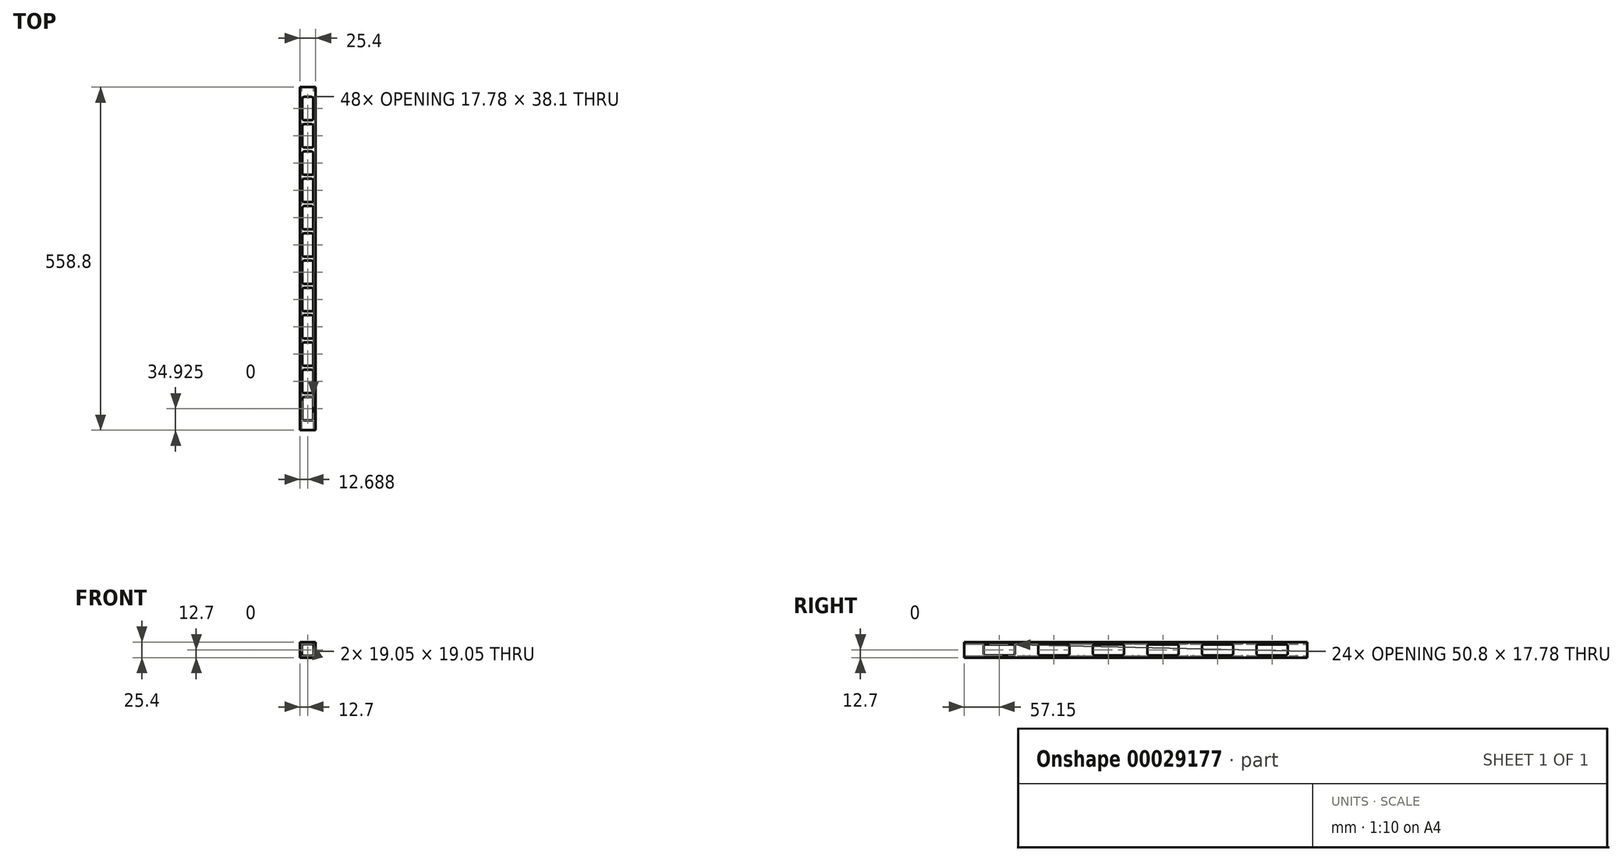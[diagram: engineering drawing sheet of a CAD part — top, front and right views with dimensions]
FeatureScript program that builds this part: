
annotation { "Feature Type Name" : "Feature", "Feature Type Description" : "" }
export const myFeature = defineFeature(function(context is Context, id is Id, definition is map)
    precondition{}
    {
        {
            var Q0;
            Q0=qCreatedBy(makeId("Front.planeOp"),FACE);
            var sketch = newSketch(context, id + "F0", { "sketchPlane" : qUnion([Q0])});
            skLineSegment(sketch, "E0.rect.bottom", {"start": v(12.7, 12.7) * mm, "end": v(-12.7, 12.7) * mm});
            skLineSegment(sketch, "E0.rect.top", {"start": v(12.7, -12.7) * mm, "end": v(-12.7, -12.7) * mm});
            skLineSegment(sketch, "E0.rect.left", {"start": v(12.7, 12.7) * mm, "end": v(12.7, -12.7) * mm});
            skLineSegment(sketch, "E0.rect.right", {"start": v(-12.7, 12.7) * mm, "end": v(-12.7, -12.7) * mm});
            skPoint(sketch, "E0.rect.middle", {"position": v(0, 0) * mm});
            skLineSegment(sketch, "E1.rect.bottom", {"start": v(9.53, 9.53) * mm, "end": v(-9.53, 9.53) * mm});
            skLineSegment(sketch, "E1.rect.top", {"start": v(9.53, -9.53) * mm, "end": v(-9.53, -9.53) * mm});
            skLineSegment(sketch, "E1.rect.left", {"start": v(9.53, 9.53) * mm, "end": v(9.53, -9.53) * mm});
            skLineSegment(sketch, "E1.rect.right", {"start": v(-9.53, 9.53) * mm, "end": v(-9.53, -9.53) * mm});
            skSolve(sketch);
        }
        {
            var Q0;
            Q0=qSketchRegion(id+"F0",true);
            extrude(context, id + "F1", {"entities" : qUnion([Q0]), "depth" : 558.8 * mm});
        }
        {
            var Q0;
            Q0=makeQuery(id+"F1.opExtrude","SWEPT_FACE",FACE,{"disambiguationData":[OSD([sQuery(id+"F0.wireOp",EDGE,"E0.rect.bottom")])]});
            var sketch = newSketch(context, id + "F2", { "sketchPlane" : qUnion([Q0])});
            skLineSegment(sketch, "E2.rect.bottom", {"start": v(5.7, -504.83) * mm, "end": v(-5.73, -504.83) * mm});
            skLineSegment(sketch, "E2.rect.top", {"start": v(5.7, -542.93) * mm, "end": v(-5.73, -542.93) * mm});
            skLineSegment(sketch, "E2.rect.left", {"start": v(8.88, -508) * mm, "end": v(8.88, -539.75) * mm});
            skLineSegment(sketch, "E2.rect.right", {"start": v(-8.9, -508) * mm, "end": v(-8.9, -539.75) * mm});
            skPoint(sketch, "E2.rect.middle", {"position": v(-0.01, -523.88) * mm});
            skPoint(sketch, "E3.visualSharp", {"position": v(-8.9, -504.83) * mm});
            skArc(sketch, "E3.filletArc", {"start": v(-5.73, -504.82) * mm, "mid": v(-7.97, -505.75) * mm, "end": v(-8.9, -508) * mm});
            skPoint(sketch, "E4.visualSharp", {"position": v(8.88, -542.93) * mm});
            skArc(sketch, "E4.filletArc", {"start": v(5.7, -542.93) * mm, "mid": v(7.95, -542) * mm, "end": v(8.88, -539.75) * mm});
            skPoint(sketch, "E5.visualSharp", {"position": v(-8.9, -542.93) * mm});
            skArc(sketch, "E5.filletArc", {"start": v(-8.9, -539.75) * mm, "mid": v(-7.97, -542) * mm, "end": v(-5.73, -542.93) * mm});
            skPoint(sketch, "E6.visualSharp", {"position": v(8.88, -504.83) * mm});
            skArc(sketch, "E6.filletArc", {"start": v(8.88, -508) * mm, "mid": v(7.95, -505.75) * mm, "end": v(5.7, -504.82) * mm});
            skLineSegment(sketch, "E7.0.1.0", {"start": v(5.7, -460.38) * mm, "end": v(-5.73, -460.38) * mm});
            skArc(sketch, "E7.0.1.1", {"start": v(-5.73, -460.38) * mm, "mid": v(-7.97, -461.3) * mm, "end": v(-8.9, -463.55) * mm});
            skLineSegment(sketch, "E7.0.1.2", {"start": v(-8.9, -463.55) * mm, "end": v(-8.9, -495.3) * mm});
            skArc(sketch, "E7.0.1.3", {"start": v(-8.9, -495.3) * mm, "mid": v(-7.97, -497.55) * mm, "end": v(-5.73, -498.48) * mm});
            skLineSegment(sketch, "E7.0.1.4", {"start": v(5.7, -498.48) * mm, "end": v(-5.73, -498.48) * mm});
            skArc(sketch, "E7.0.1.5", {"start": v(5.7, -498.48) * mm, "mid": v(7.95, -497.55) * mm, "end": v(8.88, -495.3) * mm});
            skLineSegment(sketch, "E7.0.1.6", {"start": v(8.88, -463.55) * mm, "end": v(8.88, -495.3) * mm});
            skArc(sketch, "E7.0.1.7", {"start": v(8.88, -463.55) * mm, "mid": v(7.95, -461.3) * mm, "end": v(5.7, -460.38) * mm});
            skLineSegment(sketch, "E7.0.2.0", {"start": v(5.7, -415.93) * mm, "end": v(-5.73, -415.93) * mm});
            skArc(sketch, "E7.0.2.1", {"start": v(-5.73, -415.93) * mm, "mid": v(-7.97, -416.85) * mm, "end": v(-8.9, -419.1) * mm});
            skLineSegment(sketch, "E7.0.2.2", {"start": v(-8.9, -419.1) * mm, "end": v(-8.9, -450.85) * mm});
            skArc(sketch, "E7.0.2.3", {"start": v(-8.9, -450.85) * mm, "mid": v(-7.97, -453.1) * mm, "end": v(-5.73, -454.03) * mm});
            skLineSegment(sketch, "E7.0.2.4", {"start": v(5.7, -454.03) * mm, "end": v(-5.73, -454.03) * mm});
            skArc(sketch, "E7.0.2.5", {"start": v(5.7, -454.03) * mm, "mid": v(7.95, -453.1) * mm, "end": v(8.88, -450.85) * mm});
            skLineSegment(sketch, "E7.0.2.6", {"start": v(8.88, -419.1) * mm, "end": v(8.88, -450.85) * mm});
            skArc(sketch, "E7.0.2.7", {"start": v(8.88, -419.1) * mm, "mid": v(7.95, -416.85) * mm, "end": v(5.7, -415.93) * mm});
            skLineSegment(sketch, "E7.0.3.0", {"start": v(5.7, -371.48) * mm, "end": v(-5.73, -371.48) * mm});
            skArc(sketch, "E7.0.3.1", {"start": v(-5.73, -371.48) * mm, "mid": v(-7.97, -372.4) * mm, "end": v(-8.9, -374.65) * mm});
            skLineSegment(sketch, "E7.0.3.2", {"start": v(-8.9, -374.65) * mm, "end": v(-8.9, -406.4) * mm});
            skArc(sketch, "E7.0.3.3", {"start": v(-8.9, -406.4) * mm, "mid": v(-7.97, -408.65) * mm, "end": v(-5.73, -409.58) * mm});
            skLineSegment(sketch, "E7.0.3.4", {"start": v(5.7, -409.58) * mm, "end": v(-5.73, -409.58) * mm});
            skArc(sketch, "E7.0.3.5", {"start": v(5.7, -409.58) * mm, "mid": v(7.95, -408.65) * mm, "end": v(8.88, -406.4) * mm});
            skLineSegment(sketch, "E7.0.3.6", {"start": v(8.88, -374.65) * mm, "end": v(8.88, -406.4) * mm});
            skArc(sketch, "E7.0.3.7", {"start": v(8.88, -374.65) * mm, "mid": v(7.95, -372.4) * mm, "end": v(5.7, -371.48) * mm});
            skLineSegment(sketch, "E7.0.4.0", {"start": v(5.7, -327.03) * mm, "end": v(-5.73, -327.03) * mm});
            skArc(sketch, "E7.0.4.1", {"start": v(-5.73, -327.03) * mm, "mid": v(-7.97, -327.95) * mm, "end": v(-8.9, -330.2) * mm});
            skLineSegment(sketch, "E7.0.4.2", {"start": v(-8.9, -330.2) * mm, "end": v(-8.9, -361.95) * mm});
            skArc(sketch, "E7.0.4.3", {"start": v(-8.9, -361.95) * mm, "mid": v(-7.97, -364.2) * mm, "end": v(-5.73, -365.13) * mm});
            skLineSegment(sketch, "E7.0.4.4", {"start": v(5.7, -365.13) * mm, "end": v(-5.73, -365.13) * mm});
            skArc(sketch, "E7.0.4.5", {"start": v(5.7, -365.13) * mm, "mid": v(7.95, -364.2) * mm, "end": v(8.88, -361.95) * mm});
            skLineSegment(sketch, "E7.0.4.6", {"start": v(8.88, -330.2) * mm, "end": v(8.88, -361.95) * mm});
            skArc(sketch, "E7.0.4.7", {"start": v(8.88, -330.2) * mm, "mid": v(7.95, -327.95) * mm, "end": v(5.7, -327.03) * mm});
            skLineSegment(sketch, "E7.0.5.0", {"start": v(5.7, -282.58) * mm, "end": v(-5.73, -282.58) * mm});
            skArc(sketch, "E7.0.5.1", {"start": v(-5.73, -282.58) * mm, "mid": v(-7.97, -283.5) * mm, "end": v(-8.9, -285.75) * mm});
            skLineSegment(sketch, "E7.0.5.2", {"start": v(-8.9, -285.75) * mm, "end": v(-8.9, -317.5) * mm});
            skArc(sketch, "E7.0.5.3", {"start": v(-8.9, -317.5) * mm, "mid": v(-7.97, -319.75) * mm, "end": v(-5.73, -320.68) * mm});
            skLineSegment(sketch, "E7.0.5.4", {"start": v(5.7, -320.68) * mm, "end": v(-5.73, -320.68) * mm});
            skArc(sketch, "E7.0.5.5", {"start": v(5.7, -320.68) * mm, "mid": v(7.95, -319.75) * mm, "end": v(8.88, -317.5) * mm});
            skLineSegment(sketch, "E7.0.5.6", {"start": v(8.88, -285.75) * mm, "end": v(8.88, -317.5) * mm});
            skArc(sketch, "E7.0.5.7", {"start": v(8.88, -285.75) * mm, "mid": v(7.95, -283.5) * mm, "end": v(5.7, -282.58) * mm});
            skLineSegment(sketch, "E7.0.6.0", {"start": v(5.7, -238.13) * mm, "end": v(-5.73, -238.13) * mm});
            skArc(sketch, "E7.0.6.1", {"start": v(-5.73, -238.13) * mm, "mid": v(-7.97, -239.05) * mm, "end": v(-8.9, -241.3) * mm});
            skLineSegment(sketch, "E7.0.6.2", {"start": v(-8.9, -241.3) * mm, "end": v(-8.9, -273.05) * mm});
            skArc(sketch, "E7.0.6.3", {"start": v(-8.9, -273.05) * mm, "mid": v(-7.97, -275.3) * mm, "end": v(-5.73, -276.23) * mm});
            skLineSegment(sketch, "E7.0.6.4", {"start": v(5.7, -276.23) * mm, "end": v(-5.73, -276.23) * mm});
            skArc(sketch, "E7.0.6.5", {"start": v(5.7, -276.23) * mm, "mid": v(7.95, -275.3) * mm, "end": v(8.88, -273.05) * mm});
            skLineSegment(sketch, "E7.0.6.6", {"start": v(8.88, -241.3) * mm, "end": v(8.88, -273.05) * mm});
            skArc(sketch, "E7.0.6.7", {"start": v(8.88, -241.3) * mm, "mid": v(7.95, -239.05) * mm, "end": v(5.7, -238.13) * mm});
            skLineSegment(sketch, "E7.0.7.0", {"start": v(5.7, -193.68) * mm, "end": v(-5.73, -193.68) * mm});
            skArc(sketch, "E7.0.7.1", {"start": v(-5.73, -193.68) * mm, "mid": v(-7.97, -194.6) * mm, "end": v(-8.9, -196.85) * mm});
            skLineSegment(sketch, "E7.0.7.2", {"start": v(-8.9, -196.85) * mm, "end": v(-8.9, -228.6) * mm});
            skArc(sketch, "E7.0.7.3", {"start": v(-8.9, -228.6) * mm, "mid": v(-7.97, -230.85) * mm, "end": v(-5.73, -231.78) * mm});
            skLineSegment(sketch, "E7.0.7.4", {"start": v(5.7, -231.78) * mm, "end": v(-5.73, -231.78) * mm});
            skArc(sketch, "E7.0.7.5", {"start": v(5.7, -231.78) * mm, "mid": v(7.95, -230.85) * mm, "end": v(8.88, -228.6) * mm});
            skLineSegment(sketch, "E7.0.7.6", {"start": v(8.88, -196.85) * mm, "end": v(8.88, -228.6) * mm});
            skArc(sketch, "E7.0.7.7", {"start": v(8.88, -196.85) * mm, "mid": v(7.95, -194.6) * mm, "end": v(5.7, -193.68) * mm});
            skLineSegment(sketch, "E7.0.8.0", {"start": v(5.7, -149.23) * mm, "end": v(-5.73, -149.23) * mm});
            skArc(sketch, "E7.0.8.1", {"start": v(-5.73, -149.23) * mm, "mid": v(-7.97, -150.15) * mm, "end": v(-8.9, -152.4) * mm});
            skLineSegment(sketch, "E7.0.8.2", {"start": v(-8.9, -152.4) * mm, "end": v(-8.9, -184.15) * mm});
            skArc(sketch, "E7.0.8.3", {"start": v(-8.9, -184.15) * mm, "mid": v(-7.97, -186.4) * mm, "end": v(-5.73, -187.33) * mm});
            skLineSegment(sketch, "E7.0.8.4", {"start": v(5.7, -187.33) * mm, "end": v(-5.73, -187.33) * mm});
            skArc(sketch, "E7.0.8.5", {"start": v(5.7, -187.33) * mm, "mid": v(7.95, -186.4) * mm, "end": v(8.88, -184.15) * mm});
            skLineSegment(sketch, "E7.0.8.6", {"start": v(8.88, -152.4) * mm, "end": v(8.88, -184.15) * mm});
            skArc(sketch, "E7.0.8.7", {"start": v(8.88, -152.4) * mm, "mid": v(7.95, -150.15) * mm, "end": v(5.7, -149.23) * mm});
            skLineSegment(sketch, "E7.0.9.0", {"start": v(5.7, -104.78) * mm, "end": v(-5.73, -104.78) * mm});
            skArc(sketch, "E7.0.9.1", {"start": v(-5.73, -104.78) * mm, "mid": v(-7.97, -105.7) * mm, "end": v(-8.9, -107.95) * mm});
            skLineSegment(sketch, "E7.0.9.2", {"start": v(-8.9, -107.95) * mm, "end": v(-8.9, -139.7) * mm});
            skArc(sketch, "E7.0.9.3", {"start": v(-8.9, -139.7) * mm, "mid": v(-7.97, -141.95) * mm, "end": v(-5.73, -142.88) * mm});
            skLineSegment(sketch, "E7.0.9.4", {"start": v(5.7, -142.88) * mm, "end": v(-5.73, -142.88) * mm});
            skArc(sketch, "E7.0.9.5", {"start": v(5.7, -142.88) * mm, "mid": v(7.95, -141.95) * mm, "end": v(8.88, -139.7) * mm});
            skLineSegment(sketch, "E7.0.9.6", {"start": v(8.88, -107.95) * mm, "end": v(8.88, -139.7) * mm});
            skArc(sketch, "E7.0.9.7", {"start": v(8.88, -107.95) * mm, "mid": v(7.95, -105.7) * mm, "end": v(5.7, -104.78) * mm});
            skLineSegment(sketch, "E7.0.10.0", {"start": v(5.7, -60.33) * mm, "end": v(-5.73, -60.33) * mm});
            skArc(sketch, "E7.0.10.1", {"start": v(-5.73, -60.33) * mm, "mid": v(-7.97, -61.25) * mm, "end": v(-8.9, -63.5) * mm});
            skLineSegment(sketch, "E7.0.10.2", {"start": v(-8.9, -63.5) * mm, "end": v(-8.9, -95.25) * mm});
            skArc(sketch, "E7.0.10.3", {"start": v(-8.9, -95.25) * mm, "mid": v(-7.97, -97.5) * mm, "end": v(-5.73, -98.43) * mm});
            skLineSegment(sketch, "E7.0.10.4", {"start": v(5.7, -98.43) * mm, "end": v(-5.73, -98.43) * mm});
            skArc(sketch, "E7.0.10.5", {"start": v(5.7, -98.43) * mm, "mid": v(7.95, -97.5) * mm, "end": v(8.88, -95.25) * mm});
            skLineSegment(sketch, "E7.0.10.6", {"start": v(8.88, -63.5) * mm, "end": v(8.88, -95.25) * mm});
            skArc(sketch, "E7.0.10.7", {"start": v(8.88, -63.5) * mm, "mid": v(7.95, -61.25) * mm, "end": v(5.7, -60.33) * mm});
            skLineSegment(sketch, "E7.0.11.0", {"start": v(5.7, -15.88) * mm, "end": v(-5.73, -15.88) * mm});
            skArc(sketch, "E7.0.11.1", {"start": v(-5.73, -15.88) * mm, "mid": v(-7.97, -16.8) * mm, "end": v(-8.9, -19.05) * mm});
            skLineSegment(sketch, "E7.0.11.2", {"start": v(-8.9, -19.05) * mm, "end": v(-8.9, -50.8) * mm});
            skArc(sketch, "E7.0.11.3", {"start": v(-8.9, -50.8) * mm, "mid": v(-7.97, -53.05) * mm, "end": v(-5.73, -53.98) * mm});
            skLineSegment(sketch, "E7.0.11.4", {"start": v(5.7, -53.98) * mm, "end": v(-5.73, -53.98) * mm});
            skArc(sketch, "E7.0.11.5", {"start": v(5.7, -53.98) * mm, "mid": v(7.95, -53.05) * mm, "end": v(8.88, -50.8) * mm});
            skLineSegment(sketch, "E7.0.11.6", {"start": v(8.88, -19.05) * mm, "end": v(8.88, -50.8) * mm});
            skArc(sketch, "E7.0.11.7", {"start": v(8.88, -19.05) * mm, "mid": v(7.95, -16.8) * mm, "end": v(5.7, -15.88) * mm});
            skLineSegment(sketch, "E7.direction1", {"start": v(-5.73, -504.83) * mm, "end": v(19.67, -504.83) * mm, "construction": true});
            skLineSegment(sketch, "E7.direction2", {"start": v(-5.73, -504.83) * mm, "end": v(-5.73, -460.38) * mm, "construction": true});
            skSolve(sketch);
        }
        {
            var Q0;
            Q0=makeQuery(id+"F2.imprint","IMPRINT",FACE,{"disambiguationData":[TD([[makeQuery(id+"F2.imprint","IMPRINT",EDGE,{"derivedFrom":sQuery(id+"F2.wireOp",EDGE,"E2.rect.bottom")}),1.0]])]});
            var Q1;
            Q1=makeQuery(id+"F2.imprint","IMPRINT",FACE,{"disambiguationData":[TD([[makeQuery(id+"F2.imprint","IMPRINT",EDGE,{"derivedFrom":sQuery(id+"F2.wireOp",EDGE,"E7.0.1.0")}),1.0]])]});
            var Q2;
            Q2=makeQuery(id+"F2.imprint","IMPRINT",FACE,{"disambiguationData":[TD([[makeQuery(id+"F2.imprint","IMPRINT",EDGE,{"derivedFrom":sQuery(id+"F2.wireOp",EDGE,"E7.0.2.0")}),1.0]])]});
            var Q3;
            Q3=makeQuery(id+"F2.imprint","IMPRINT",FACE,{"disambiguationData":[TD([[makeQuery(id+"F2.imprint","IMPRINT",EDGE,{"derivedFrom":sQuery(id+"F2.wireOp",EDGE,"E7.0.3.0")}),1.0]])]});
            var Q4;
            Q4=makeQuery(id+"F2.imprint","IMPRINT",FACE,{"disambiguationData":[TD([[makeQuery(id+"F2.imprint","IMPRINT",EDGE,{"derivedFrom":sQuery(id+"F2.wireOp",EDGE,"E7.0.4.0")}),1.0]])]});
            var Q5;
            Q5=makeQuery(id+"F2.imprint","IMPRINT",FACE,{"disambiguationData":[TD([[makeQuery(id+"F2.imprint","IMPRINT",EDGE,{"derivedFrom":sQuery(id+"F2.wireOp",EDGE,"E7.0.5.0")}),1.0]])]});
            var Q6;
            Q6=makeQuery(id+"F2.imprint","IMPRINT",FACE,{"disambiguationData":[TD([[makeQuery(id+"F2.imprint","IMPRINT",EDGE,{"derivedFrom":sQuery(id+"F2.wireOp",EDGE,"E7.0.6.0")}),1.0]])]});
            var Q7;
            Q7=makeQuery(id+"F2.imprint","IMPRINT",FACE,{"disambiguationData":[TD([[makeQuery(id+"F2.imprint","IMPRINT",EDGE,{"derivedFrom":sQuery(id+"F2.wireOp",EDGE,"E7.0.7.0")}),1.0]])]});
            var Q8;
            Q8=makeQuery(id+"F2.imprint","IMPRINT",FACE,{"disambiguationData":[TD([[makeQuery(id+"F2.imprint","IMPRINT",EDGE,{"derivedFrom":sQuery(id+"F2.wireOp",EDGE,"E7.0.8.0")}),1.0]])]});
            var Q9;
            Q9=makeQuery(id+"F2.imprint","IMPRINT",FACE,{"disambiguationData":[TD([[makeQuery(id+"F2.imprint","IMPRINT",EDGE,{"derivedFrom":sQuery(id+"F2.wireOp",EDGE,"E7.0.9.0")}),1.0]])]});
            var Q10;
            Q10=makeQuery(id+"F2.imprint","IMPRINT",FACE,{"disambiguationData":[TD([[makeQuery(id+"F2.imprint","IMPRINT",EDGE,{"derivedFrom":sQuery(id+"F2.wireOp",EDGE,"E7.0.10.0")}),1.0]])]});
            var Q11;
            Q11=makeQuery(id+"F2.imprint","IMPRINT",FACE,{"disambiguationData":[TD([[makeQuery(id+"F2.imprint","IMPRINT",EDGE,{"derivedFrom":sQuery(id+"F2.wireOp",EDGE,"E7.0.11.0")}),1.0]])]});
            extrude(context, id + "F3", {"entities" : qUnion([Q0, Q1, Q2, Q3, Q4, Q5, Q6, Q7, Q8, Q9, Q10, Q11]), "operationType" : NewBodyOperationType.REMOVE, "oppositeDirection" : true, "depth" : 25.4 * mm});
        }
        {
            var Q0;
            Q0=makeQuery(id+"F1.opExtrude","SWEPT_FACE",FACE,{"disambiguationData":[OSD([sQuery(id+"F0.wireOp",EDGE,"E0.rect.left")])]});
            var sketch = newSketch(context, id + "F4", { "sketchPlane" : qUnion([Q0])});
            skLineSegment(sketch, "E8", {"start": v(-558.8, 0) * mm, "end": v(-527.05, 0) * mm});
            skLineSegment(sketch, "E9.rect.bottom", {"start": v(-479.43, -8.89) * mm, "end": v(-523.88, -8.89) * mm});
            skLineSegment(sketch, "E9.rect.top", {"start": v(-479.43, 8.9) * mm, "end": v(-523.88, 8.9) * mm});
            skLineSegment(sketch, "E9.rect.left", {"start": v(-476.25, -5.71) * mm, "end": v(-476.25, 5.72) * mm});
            skLineSegment(sketch, "E9.rect.right", {"start": v(-527.05, -5.71) * mm, "end": v(-527.05, 5.72) * mm});
            skPoint(sketch, "E9.rect.middle", {"position": v(-501.65, 0) * mm});
            skPoint(sketch, "E10.visualSharp", {"position": v(-476.25, 8.9) * mm});
            skArc(sketch, "E10.filletArc", {"start": v(-476.25, 5.72) * mm, "mid": v(-477.18, 7.96) * mm, "end": v(-479.43, 8.9) * mm});
            skPoint(sketch, "E11.visualSharp", {"position": v(-476.25, -8.89) * mm});
            skArc(sketch, "E11.filletArc", {"start": v(-479.43, -8.89) * mm, "mid": v(-477.18, -7.96) * mm, "end": v(-476.25, -5.71) * mm});
            skPoint(sketch, "E12.visualSharp", {"position": v(-527.05, -8.89) * mm});
            skArc(sketch, "E12.filletArc", {"start": v(-527.05, -5.71) * mm, "mid": v(-526.12, -7.96) * mm, "end": v(-523.88, -8.89) * mm});
            skPoint(sketch, "E13.visualSharp", {"position": v(-527.05, 8.9) * mm});
            skArc(sketch, "E13.filletArc", {"start": v(-523.88, 8.9) * mm, "mid": v(-526.12, 7.96) * mm, "end": v(-527.05, 5.72) * mm});
            skLineSegment(sketch, "E14.1.0.0", {"start": v(-387.35, -5.71) * mm, "end": v(-387.35, 5.72) * mm});
            skArc(sketch, "E14.1.0.1", {"start": v(-387.35, 5.72) * mm, "mid": v(-388.28, 7.96) * mm, "end": v(-390.52, 8.9) * mm});
            skLineSegment(sketch, "E14.1.0.2", {"start": v(-390.52, 8.9) * mm, "end": v(-434.97, 8.9) * mm});
            skArc(sketch, "E14.1.0.3", {"start": v(-434.97, 8.9) * mm, "mid": v(-437.22, 7.96) * mm, "end": v(-438.15, 5.72) * mm});
            skLineSegment(sketch, "E14.1.0.4", {"start": v(-438.15, -5.71) * mm, "end": v(-438.15, 5.72) * mm});
            skArc(sketch, "E14.1.0.5", {"start": v(-438.15, -5.71) * mm, "mid": v(-437.22, -7.96) * mm, "end": v(-434.97, -8.89) * mm});
            skLineSegment(sketch, "E14.1.0.6", {"start": v(-390.52, -8.89) * mm, "end": v(-434.97, -8.89) * mm});
            skArc(sketch, "E14.1.0.7", {"start": v(-390.52, -8.89) * mm, "mid": v(-388.28, -7.96) * mm, "end": v(-387.35, -5.71) * mm});
            skLineSegment(sketch, "E14.2.0.0", {"start": v(-298.45, -5.71) * mm, "end": v(-298.45, 5.72) * mm});
            skArc(sketch, "E14.2.0.1", {"start": v(-298.45, 5.72) * mm, "mid": v(-299.38, 7.96) * mm, "end": v(-301.62, 8.9) * mm});
            skLineSegment(sketch, "E14.2.0.2", {"start": v(-301.62, 8.9) * mm, "end": v(-346.07, 8.9) * mm});
            skArc(sketch, "E14.2.0.3", {"start": v(-346.07, 8.9) * mm, "mid": v(-348.32, 7.96) * mm, "end": v(-349.25, 5.72) * mm});
            skLineSegment(sketch, "E14.2.0.4", {"start": v(-349.25, -5.71) * mm, "end": v(-349.25, 5.72) * mm});
            skArc(sketch, "E14.2.0.5", {"start": v(-349.25, -5.71) * mm, "mid": v(-348.32, -7.96) * mm, "end": v(-346.07, -8.89) * mm});
            skLineSegment(sketch, "E14.2.0.6", {"start": v(-301.62, -8.89) * mm, "end": v(-346.07, -8.89) * mm});
            skArc(sketch, "E14.2.0.7", {"start": v(-301.62, -8.89) * mm, "mid": v(-299.38, -7.96) * mm, "end": v(-298.45, -5.71) * mm});
            skLineSegment(sketch, "E14.3.0.0", {"start": v(-209.55, -5.71) * mm, "end": v(-209.55, 5.72) * mm});
            skArc(sketch, "E14.3.0.1", {"start": v(-209.55, 5.72) * mm, "mid": v(-210.48, 7.96) * mm, "end": v(-212.72, 8.9) * mm});
            skLineSegment(sketch, "E14.3.0.2", {"start": v(-212.72, 8.9) * mm, "end": v(-257.17, 8.9) * mm});
            skArc(sketch, "E14.3.0.3", {"start": v(-257.17, 8.9) * mm, "mid": v(-259.42, 7.96) * mm, "end": v(-260.35, 5.72) * mm});
            skLineSegment(sketch, "E14.3.0.4", {"start": v(-260.35, -5.71) * mm, "end": v(-260.35, 5.72) * mm});
            skArc(sketch, "E14.3.0.5", {"start": v(-260.35, -5.71) * mm, "mid": v(-259.42, -7.96) * mm, "end": v(-257.17, -8.89) * mm});
            skLineSegment(sketch, "E14.3.0.6", {"start": v(-212.72, -8.89) * mm, "end": v(-257.17, -8.89) * mm});
            skArc(sketch, "E14.3.0.7", {"start": v(-212.72, -8.89) * mm, "mid": v(-210.48, -7.96) * mm, "end": v(-209.55, -5.71) * mm});
            skLineSegment(sketch, "E14.4.0.0", {"start": v(-120.65, -5.71) * mm, "end": v(-120.65, 5.72) * mm});
            skArc(sketch, "E14.4.0.1", {"start": v(-120.65, 5.72) * mm, "mid": v(-121.58, 7.96) * mm, "end": v(-123.82, 8.9) * mm});
            skLineSegment(sketch, "E14.4.0.2", {"start": v(-123.82, 8.9) * mm, "end": v(-168.27, 8.9) * mm});
            skArc(sketch, "E14.4.0.3", {"start": v(-168.27, 8.9) * mm, "mid": v(-170.52, 7.96) * mm, "end": v(-171.45, 5.72) * mm});
            skLineSegment(sketch, "E14.4.0.4", {"start": v(-171.45, -5.71) * mm, "end": v(-171.45, 5.72) * mm});
            skArc(sketch, "E14.4.0.5", {"start": v(-171.45, -5.71) * mm, "mid": v(-170.52, -7.96) * mm, "end": v(-168.27, -8.89) * mm});
            skLineSegment(sketch, "E14.4.0.6", {"start": v(-123.82, -8.89) * mm, "end": v(-168.27, -8.89) * mm});
            skArc(sketch, "E14.4.0.7", {"start": v(-123.82, -8.89) * mm, "mid": v(-121.58, -7.96) * mm, "end": v(-120.65, -5.71) * mm});
            skLineSegment(sketch, "E14.5.0.0", {"start": v(-31.75, -5.71) * mm, "end": v(-31.75, 5.72) * mm});
            skArc(sketch, "E14.5.0.1", {"start": v(-31.75, 5.72) * mm, "mid": v(-32.68, 7.96) * mm, "end": v(-34.92, 8.9) * mm});
            skLineSegment(sketch, "E14.5.0.2", {"start": v(-34.92, 8.9) * mm, "end": v(-79.37, 8.9) * mm});
            skArc(sketch, "E14.5.0.3", {"start": v(-79.37, 8.9) * mm, "mid": v(-81.62, 7.96) * mm, "end": v(-82.55, 5.72) * mm});
            skLineSegment(sketch, "E14.5.0.4", {"start": v(-82.55, -5.71) * mm, "end": v(-82.55, 5.72) * mm});
            skArc(sketch, "E14.5.0.5", {"start": v(-82.55, -5.71) * mm, "mid": v(-81.62, -7.96) * mm, "end": v(-79.37, -8.89) * mm});
            skLineSegment(sketch, "E14.5.0.6", {"start": v(-34.92, -8.89) * mm, "end": v(-79.37, -8.89) * mm});
            skArc(sketch, "E14.5.0.7", {"start": v(-34.92, -8.89) * mm, "mid": v(-32.68, -7.96) * mm, "end": v(-31.75, -5.71) * mm});
            skLineSegment(sketch, "E14.direction1", {"start": v(-476.25, -5.71) * mm, "end": v(-387.35, -5.71) * mm, "construction": true});
            skLineSegment(sketch, "E15.trimOffspring", {"start": v(-476.25, 0) * mm, "end": v(0, 0) * mm});
            skSolve(sketch);
        }
        {
            var Q0;
            Q0 = qSketchRegion(id + "F4", true);
            extrude(context, id + "F5", {"entities" : qUnion([Q0]), "operationType" : NewBodyOperationType.REMOVE, "oppositeDirection" : true, "depth" : 25.4 * mm});
        }
    });
